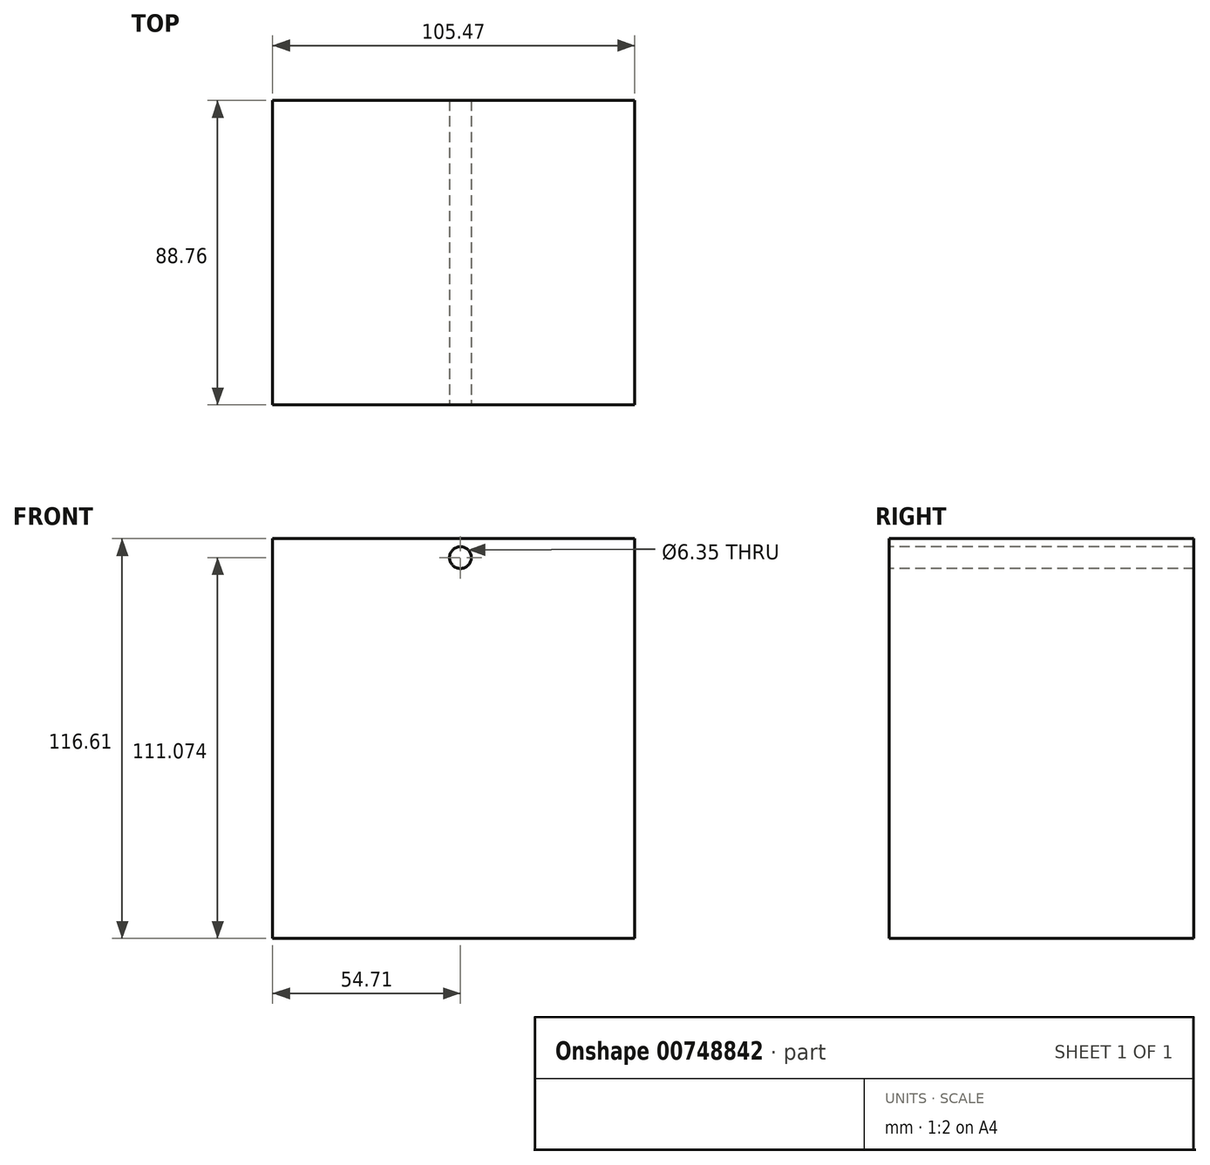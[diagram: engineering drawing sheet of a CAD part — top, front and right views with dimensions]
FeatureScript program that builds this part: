
annotation { "Feature Type Name" : "Feature", "Feature Type Description" : "" }
export const myFeature = defineFeature(function(context is Context, id is Id, definition is map)
    precondition{}
    {
        {
            var Q0;
            Q0=qCreatedBy(makeId("Front.planeOp"),FACE);
            var sketch = newSketch(context, id + "F0", { "sketchPlane" : qUnion([Q0])});
            skLineSegment(sketch, "E0.bottom", {"start": v(-54.71, -60.91) * mm, "end": v(50.76, -60.91) * mm});
            skLineSegment(sketch, "E0.top", {"start": v(-54.71, 55.7) * mm, "end": v(50.76, 55.7) * mm});
            skLineSegment(sketch, "E0.left", {"start": v(-54.71, -60.91) * mm, "end": v(-54.71, 55.7) * mm});
            skLineSegment(sketch, "E0.right", {"start": v(50.76, -60.91) * mm, "end": v(50.76, 55.7) * mm});
            skSolve(sketch);
        }
        {
            var Q0;
            Q0=makeQuery(id+"F0.imprint","IMPRINT",FACE,{"disambiguationData":[TD([[makeQuery(id+"F0.imprint","IMPRINT",EDGE,{"derivedFrom":sQuery(id+"F0.wireOp",EDGE,"E0.bottom")}),1.0]])]});
            extrude(context, id + "F1", {"entities" : qUnion([Q0]), "depth" : 88.76 * mm, "offsetDistance" : 25.4 * mm});
        }
        {
            var Q0;
            Q0=makeQuery(id+"F1.opExtrude","CAP_FACE",FACE,{"disambiguationData":[OSD([sQuery(id+"F0.wireOp",EDGE,"E0.bottom"),sQuery(id+"F0.wireOp",EDGE,"E0.top"),sQuery(id+"F0.wireOp",EDGE,"E0.left"),sQuery(id+"F0.wireOp",EDGE,"E0.right")])],"isStart":false});
            var sketch = newSketch(context, id + "F2", { "sketchPlane" : qUnion([Q0])});
            skPoint(sketch, "E1", {"position": v(-47.27, 0) * mm});
            skSolve(sketch);
        }
        {
            var Q0;
            Q0=makeQuery(id+"F2.imprint","IMPRINT",FACE,{"disambiguationData":[TD([[makeQuery(id+"F2.imprint","IMPRINT",EDGE,{"derivedFrom":makeQuery(id+"F1.opExtrude","CAP_EDGE",EDGE,{"disambiguationData":[OSD([sQuery(id+"F0.wireOp",EDGE,"E0.bottom")])],"isStart":false})}),1.0]])]});
            var sketch = newSketch(context, id + "F3", { "sketchPlane" : qUnion([Q0])});
            skPoint(sketch, "E2", {"position": v(0, 50.16) * mm});
            skSolve(sketch);
        }
        {
            var Q0;
            Q0=sQuery(id+"F3.wireOp",VERTEX,"E2");
            var Q1;
            Q1=makeQuery(id+"F1.opExtrude","SWEPT_BODY",BODY,{"disambiguationData":[OSD([sQuery(id+"F0.wireOp",EDGE,"E0.bottom"),sQuery(id+"F0.wireOp",EDGE,"E0.top"),sQuery(id+"F0.wireOp",EDGE,"E0.left"),sQuery(id+"F0.wireOp",EDGE,"E0.right")])]});
            hole(context, id + "F4", {"style" : HoleStyle.SIMPLE, "endStyle" : HoleEndStyle.THROUGH, "holeDiameter" : 6.35 * mm, "majorDiameter" : 6.35 * mm, "isTappedThrough" : true, "tappedDepth" : 12.7 * mm, "tapClearance" : 3, "locations" : qUnion([Q0]), "scope" : qUnion([Q1])});
        }
    });
